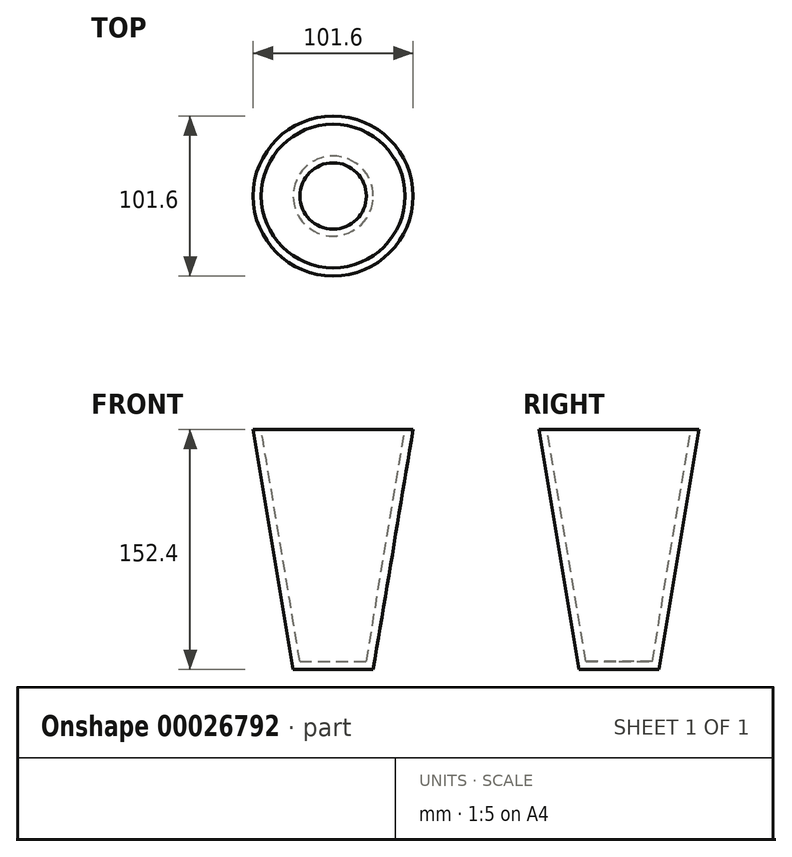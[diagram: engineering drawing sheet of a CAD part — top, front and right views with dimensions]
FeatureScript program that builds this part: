
annotation { "Feature Type Name" : "Feature", "Feature Type Description" : "" }
export const myFeature = defineFeature(function(context is Context, id is Id, definition is map)
    precondition{}
    {
        {
            var Q0;
            Q0=qCreatedBy(makeId("Front.planeOp"),FACE);
            var sketch = newSketch(context, id + "F0", { "sketchPlane" : qUnion([Q0])});
            skLineSegment(sketch, "E0", {"start": v(-50.8, 95.94) * mm, "end": v(0, 95.94) * mm});
            skLineSegment(sketch, "E1", {"start": v(-50.8, 95.94) * mm, "end": v(-25.4, -56.46) * mm});
            skLineSegment(sketch, "E2", {"start": v(-25.4, -56.46) * mm, "end": v(0, -56.46) * mm});
            skPoint(sketch, "E3.end.orphan", {"position": v(97.83, 95.94) * mm});
            skPoint(sketch, "E3.start.orphan", {"position": v(76.3, -56.46) * mm});
            skLineSegment(sketch, "E4", {"start": v(0, 95.94) * mm, "end": v(0, -56.46) * mm});
            skSolve(sketch);
        }
        {
            var Q0;
            Q0=makeQuery(id+"F0.imprint","IMPRINT",FACE,{"disambiguationData":[TD([[makeQuery(id+"F0.imprint","IMPRINT",EDGE,{"derivedFrom":sQuery(id+"F0.wireOp",EDGE,"E0")}),-1.0]])]});
            var Q1;
            Q1=sQuery(id+"F0.wireOp",EDGE,"E4");
            revolve(context, id + "F1", {"entities" : qUnion([Q0]), "axis" : qUnion([Q1]), "revolveType" : RevolveType.FULL});
        }
        {
            var Q0;
            Q0=makeQuery(id+"F1.opRevolve","SWEPT_FACE",FACE,{"disambiguationData":[OSD([sQuery(id+"F0.wireOp",EDGE,"E0")])]});
            shell(context, id + "F2", {"entities" : qUnion([Q0]), "thickness" : 5.08 * mm});
        }
    });
